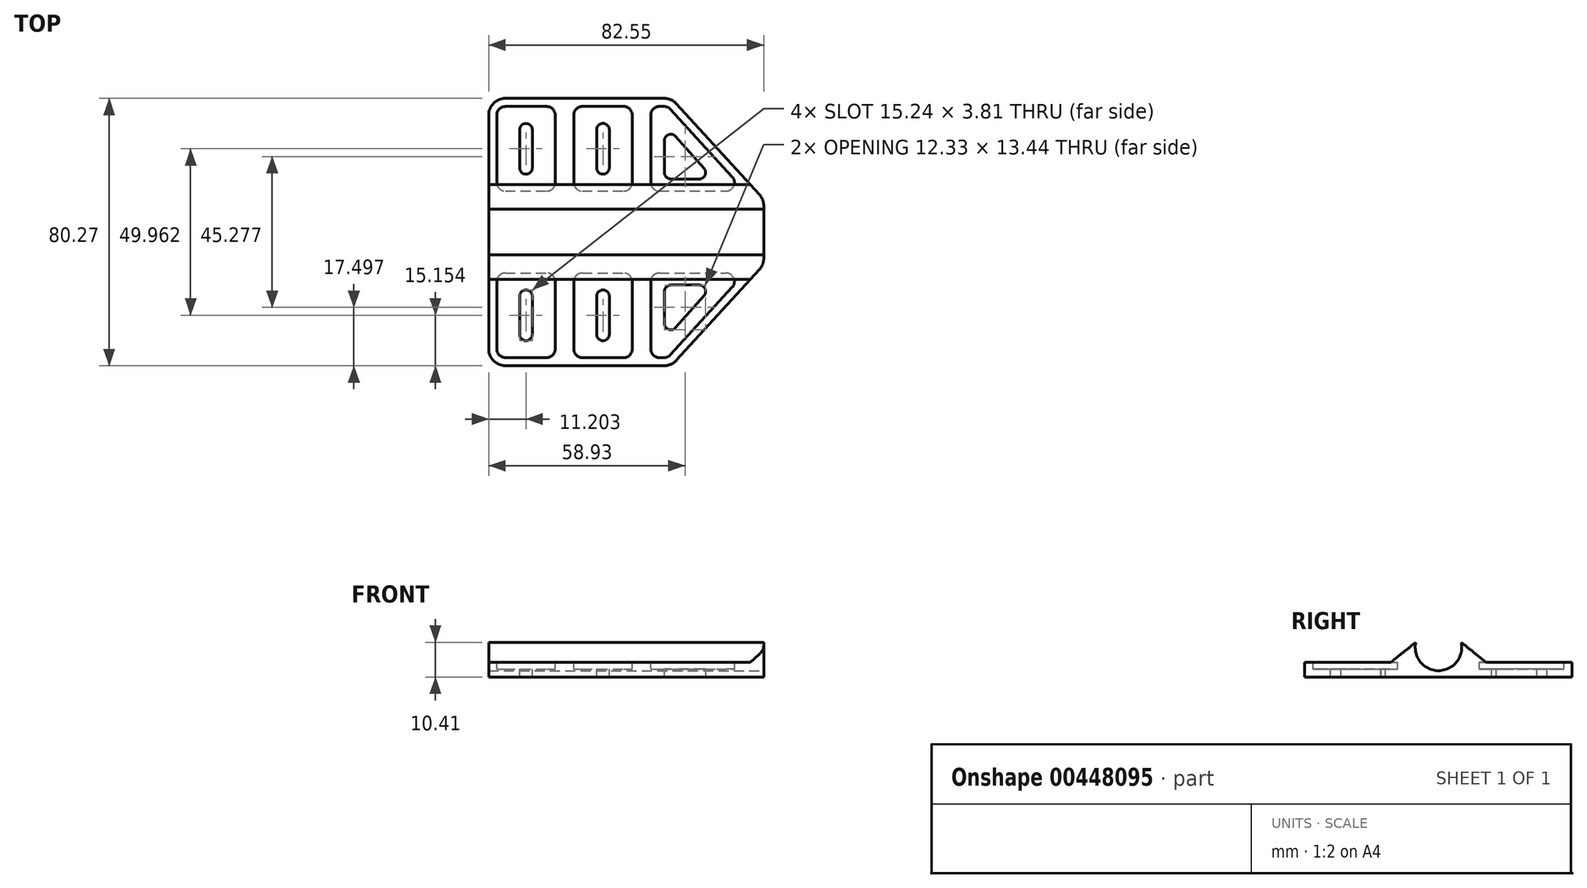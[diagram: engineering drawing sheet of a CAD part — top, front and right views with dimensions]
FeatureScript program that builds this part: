
annotation { "Feature Type Name" : "Feature", "Feature Type Description" : "" }
export const myFeature = defineFeature(function(context is Context, id is Id, definition is map)
    precondition{}
    {
        {
            var Q0;
            Q0=qCreatedBy(makeId("Top.planeOp"),FACE);
            var sketch = newSketch(context, id + "F0", { "sketchPlane" : qUnion([Q0])});
            skLineSegment(sketch, "E0.bottom", {"start": v(-50.59, 33.3) * mm, "end": v(4.28, 33.3) * mm});
            skLineSegment(sketch, "E0.top", {"start": v(-50.59, -46.96) * mm, "end": v(4.28, -46.96) * mm});
            skLineSegment(sketch, "E0.left", {"start": v(-50.59, 33.3) * mm, "end": v(-50.59, -46.96) * mm});
            skLineSegment(sketch, "E0.right", {"start": v(4.28, 33.3) * mm, "end": v(4.28, -46.96) * mm});
            skLineSegment(sketch, "E1", {"start": v(4.28, 3.02) * mm, "end": v(31.96, 3.02) * mm});
            skLineSegment(sketch, "E2", {"start": v(4.28, -16.67) * mm, "end": v(31.96, -16.67) * mm});
            skLineSegment(sketch, "E3", {"start": v(4.28, 33.3) * mm, "end": v(31.96, 3.02) * mm});
            skLineSegment(sketch, "E4", {"start": v(4.28, -46.96) * mm, "end": v(31.96, -16.67) * mm});
            skLineSegment(sketch, "E5", {"start": v(31.96, -16.67) * mm, "end": v(31.96, 3.02) * mm});
            skSolve(sketch);
        }
        {
            var Q0;
            Q0 = qSketchRegion(id + "F0", true);
            extrude(context, id + "F1", {"entities" : qUnion([Q0]), "depth" : 4.44 * mm});
        }
        {
            var Q0;
            Q0=makeQuery(id+"F1.opExtrude","CAP_FACE",FACE,{"disambiguationData":[OSD([sQuery(id+"F0.wireOp",EDGE,"E0.bottom"),sQuery(id+"F0.wireOp",EDGE,"E0.top"),sQuery(id+"F0.wireOp",EDGE,"E0.left"),sQuery(id+"F0.wireOp",EDGE,"E3"),sQuery(id+"F0.wireOp",EDGE,"E4"),sQuery(id+"F0.wireOp",EDGE,"E5")])],"isStart":false});
            var sketch = newSketch(context, id + "F2", { "sketchPlane" : qUnion([Q0])});
            skLineSegment(sketch, "E6", {"start": v(31.96, 3.02) * mm, "end": v(-50.59, 3.02) * mm});
            skLineSegment(sketch, "E7", {"start": v(31.96, -16.67) * mm, "end": v(-50.59, -16.67) * mm});
            skLineSegment(sketch, "E8", {"start": v(31.96, -6.83) * mm, "end": v(-50.59, -6.83) * mm});
            skSolve(sketch);
        }
        {
            var Q0;
            Q0=makeQuery(id+"F1.opExtrude","SWEPT_FACE",FACE,{"disambiguationData":[OSD([sQuery(id+"F0.wireOp",EDGE,"E5")])]});
            var sketch = newSketch(context, id + "F3", { "sketchPlane" : qUnion([Q0])});
            skCircle(sketch, "E9", {"center": v(-6.83, 8.9) * mm, "radius": 6.99 * mm});
            skPoint(sketch, "E9.centerSnap0", {"position": v(-6.83, 4.45) * mm});
            skSolve(sketch);
        }
        {
            var Q0;
            {var subQ0=sQuery(id+"F3.wireOp",EDGE,"E9");var subQ1=makeQuery(id+"F1.opExtrude","CAP_EDGE",EDGE,{"disambiguationData":[OSD([sQuery(id+"F0.wireOp",EDGE,"E5")])],"isStart":false});var subQ2=makeQuery(id+"F3.imprint","INTERSECT",VERTEX,{"disambiguationData":[OD(0.0)],"derivedFrom":[subQ1,subQ0]});Q0=makeQuery(id+"F3.imprint","IMPRINT",FACE,{"disambiguationData":[TD([[makeQuery(id+"F3.imprint","IMPRINT",EDGE,{"disambiguationData":[TD([[subQ2,-1.0]])],"derivedFrom":subQ0}),1.0]])]});}
            var Q1;
            {var subQ0=sQuery(id+"F3.wireOp",EDGE,"E9");var subQ1=makeQuery(id+"F1.opExtrude","CAP_EDGE",EDGE,{"disambiguationData":[OSD([sQuery(id+"F0.wireOp",EDGE,"E5")])],"isStart":false});var subQ2=makeQuery(id+"F3.imprint","INTERSECT",VERTEX,{"disambiguationData":[OD(0.0)],"derivedFrom":[subQ1,subQ0]});Q1=makeQuery(id+"F3.imprint","IMPRINT",FACE,{"disambiguationData":[TD([[makeQuery(id+"F3.imprint","IMPRINT",EDGE,{"disambiguationData":[TD([[subQ2,1.0]])],"derivedFrom":subQ0}),1.0]])]});}
            extrude(context, id + "F4", {"entities" : qUnion([Q0, Q1]), "operationType" : NewBodyOperationType.ADD, "oppositeDirection" : true, "depth" : 82.55 * mm});
        }
        {
            var Q0;
            Q0=makeQuery(id+"F4.boolean.opBoolean","INTERSECT",EDGE,{"disambiguationData":[OD(1.0)],"derivedFrom":[makeQuery(id+"F1.opExtrude","CAP_FACE",FACE,{"disambiguationData":[OSD([sQuery(id+"F0.wireOp",EDGE,"E0.bottom"),sQuery(id+"F0.wireOp",EDGE,"E0.top"),sQuery(id+"F0.wireOp",EDGE,"E0.left"),sQuery(id+"F0.wireOp",EDGE,"E3"),sQuery(id+"F0.wireOp",EDGE,"E4"),sQuery(id+"F0.wireOp",EDGE,"E5")])],"isStart":false}),makeQuery(id+"F4.opExtrude","SWEPT_FACE",FACE,{"disambiguationData":[OSD([sQuery(id+"F3.wireOp",EDGE,"E9")])]})]});
            var Q1;
            Q1=makeQuery(id+"F4.boolean.opBoolean","INTERSECT",EDGE,{"disambiguationData":[OD(0.0)],"derivedFrom":[makeQuery(id+"F1.opExtrude","CAP_FACE",FACE,{"disambiguationData":[OSD([sQuery(id+"F0.wireOp",EDGE,"E0.bottom"),sQuery(id+"F0.wireOp",EDGE,"E0.top"),sQuery(id+"F0.wireOp",EDGE,"E0.left"),sQuery(id+"F0.wireOp",EDGE,"E3"),sQuery(id+"F0.wireOp",EDGE,"E4"),sQuery(id+"F0.wireOp",EDGE,"E5")])],"isStart":false}),makeQuery(id+"F4.opExtrude","SWEPT_FACE",FACE,{"disambiguationData":[OSD([sQuery(id+"F3.wireOp",EDGE,"E9")])]})]});
            chamfer(context, id + "F5", {"entities" : qUnion([Q0, Q1]), "width" : 7.62 * mm, "tangentPropagation" : true});
        }
        {
            var Q0;
            Q0 = qSketchRegion(id + "F3", true);
            extrude(context, id + "F6", {"entities" : qUnion([Q0]), "operationType" : NewBodyOperationType.REMOVE, "oppositeDirection" : true, "depth" : 101.6 * mm});
        }
        {
            var Q0;
            {var subQ0=sQuery(id+"F2.wireOp",EDGE,"E7");Q0=makeQuery(id+"F2.imprint","IMPRINT",FACE,{"disambiguationData":[TD([[makeQuery(id+"F2.imprint","IMPRINT",EDGE,{"derivedFrom":subQ0}),1.0]])]});}
            var sketch = newSketch(context, id + "F7", { "sketchPlane" : qUnion([Q0])});
            skLineSegment(sketch, "E10.bottom", {"start": v(-48.15, -19.1) * mm, "end": v(-30.62, -19.1) * mm});
            skLineSegment(sketch, "E10.top", {"start": v(-48.15, -44.5) * mm, "end": v(-30.62, -44.5) * mm});
            skLineSegment(sketch, "E10.left", {"start": v(-48.15, -19.1) * mm, "end": v(-48.15, -44.5) * mm});
            skLineSegment(sketch, "E10.right", {"start": v(-30.62, -19.1) * mm, "end": v(-30.62, -44.5) * mm});
            skLineSegment(sketch, "E11.bottom", {"start": v(-25.04, -44.52) * mm, "end": v(-7.51, -44.52) * mm});
            skLineSegment(sketch, "E11.top", {"start": v(-25.04, -19.12) * mm, "end": v(-7.51, -19.12) * mm});
            skLineSegment(sketch, "E11.left", {"start": v(-25.04, -44.52) * mm, "end": v(-25.04, -19.12) * mm});
            skLineSegment(sketch, "E11.right", {"start": v(-7.51, -44.52) * mm, "end": v(-7.51, -19.12) * mm});
            skLineSegment(sketch, "E12", {"start": v(-1.92, -19.12) * mm, "end": v(-1.92, -44.52) * mm});
            skLineSegment(sketch, "E13", {"start": v(-1.92, -19.12) * mm, "end": v(26.42, -19.12) * mm});
            skLineSegment(sketch, "E14", {"start": v(-1.92, -44.52) * mm, "end": v(3.2, -44.52) * mm});
            skLineSegment(sketch, "E15", {"start": v(3.2, -44.52) * mm, "end": v(26.42, -19.12) * mm});
            skLineSegment(sketch, "E16.MirrorCS", {"start": v(-1.92, 30.87) * mm, "end": v(3.2, 30.87) * mm});
            skLineSegment(sketch, "E17.MirrorCS", {"start": v(-48.15, 30.86) * mm, "end": v(-30.62, 30.86) * mm});
            skLineSegment(sketch, "E18.MirrorCS", {"start": v(-48.15, 5.46) * mm, "end": v(-30.62, 5.46) * mm});
            skLineSegment(sketch, "E19.MirrorCS", {"start": v(-30.62, 5.46) * mm, "end": v(-30.62, 30.86) * mm});
            skLineSegment(sketch, "E20.MirrorCS", {"start": v(-1.92, 5.47) * mm, "end": v(26.42, 5.47) * mm});
            skLineSegment(sketch, "E21.MirrorCS", {"start": v(-1.92, 5.47) * mm, "end": v(-1.92, 30.87) * mm});
            skLineSegment(sketch, "E22.MirrorCS", {"start": v(-7.51, 30.87) * mm, "end": v(-7.51, 5.47) * mm});
            skLineSegment(sketch, "E23.MirrorCS", {"start": v(3.2, 30.87) * mm, "end": v(26.42, 5.47) * mm});
            skLineSegment(sketch, "E24.MirrorCS", {"start": v(-25.04, 30.87) * mm, "end": v(-7.51, 30.87) * mm});
            skLineSegment(sketch, "E25.MirrorCS", {"start": v(-48.15, 5.46) * mm, "end": v(-48.15, 30.86) * mm});
            skLineSegment(sketch, "E26.MirrorCS", {"start": v(-25.04, 5.47) * mm, "end": v(-7.51, 5.47) * mm});
            skLineSegment(sketch, "E27.MirrorCS", {"start": v(-25.04, 30.87) * mm, "end": v(-25.04, 5.47) * mm});
            skSolve(sketch);
        }
        {
            var Q0;
            Q0 = qSketchRegion(id + "F7", true);
            extrude(context, id + "F8", {"entities" : qUnion([Q0]), "operationType" : NewBodyOperationType.REMOVE, "oppositeDirection" : true, "depth" : 2.03 * mm});
        }
        {
            var Q0;
            Q0=makeQuery(id+"F8.boolean.opBoolean","COPY",EDGE,{"derivedFrom":makeQuery(id+"F8.opExtrude","SWEPT_EDGE",EDGE,{"disambiguationData":[OSD([sQuery(id+"F7.wireOp",EDGE,"E10.bottom"),sQuery(id+"F7.wireOp",EDGE,"E10.left")])]})});
            var Q1;
            Q1=makeQuery(id+"F8.boolean.opBoolean","COPY",EDGE,{"derivedFrom":makeQuery(id+"F8.opExtrude","SWEPT_EDGE",EDGE,{"disambiguationData":[OSD([sQuery(id+"F7.wireOp",EDGE,"E17.MirrorCS"),sQuery(id+"F7.wireOp",EDGE,"E25.MirrorCS")])]})});
            var Q2;
            Q2=makeQuery(id+"F8.boolean.opBoolean","COPY",EDGE,{"derivedFrom":makeQuery(id+"F8.opExtrude","SWEPT_EDGE",EDGE,{"disambiguationData":[OSD([sQuery(id+"F7.wireOp",EDGE,"E24.MirrorCS"),sQuery(id+"F7.wireOp",EDGE,"E27.MirrorCS")])]})});
            var Q3;
            Q3=makeQuery(id+"F8.boolean.opBoolean","COPY",EDGE,{"derivedFrom":makeQuery(id+"F8.opExtrude","SWEPT_EDGE",EDGE,{"disambiguationData":[OSD([sQuery(id+"F7.wireOp",EDGE,"E16.MirrorCS"),sQuery(id+"F7.wireOp",EDGE,"E21.MirrorCS")])]})});
            var Q4;
            Q4=makeQuery(id+"F8.boolean.opBoolean","COPY",EDGE,{"derivedFrom":makeQuery(id+"F8.opExtrude","SWEPT_EDGE",EDGE,{"disambiguationData":[OSD([sQuery(id+"F7.wireOp",EDGE,"E16.MirrorCS"),sQuery(id+"F7.wireOp",EDGE,"E23.MirrorCS")])]})});
            var Q5;
            Q5=makeQuery(id+"F8.boolean.opBoolean","COPY",EDGE,{"derivedFrom":makeQuery(id+"F8.opExtrude","SWEPT_EDGE",EDGE,{"disambiguationData":[OSD([sQuery(id+"F7.wireOp",EDGE,"E12"),sQuery(id+"F7.wireOp",EDGE,"E13")])]})});
            var Q6;
            Q6=makeQuery(id+"F8.boolean.opBoolean","COPY",EDGE,{"derivedFrom":makeQuery(id+"F8.opExtrude","SWEPT_EDGE",EDGE,{"disambiguationData":[OSD([sQuery(id+"F7.wireOp",EDGE,"E11.top"),sQuery(id+"F7.wireOp",EDGE,"E11.left")])]})});
            var Q7;
            Q7=makeQuery(id+"F8.boolean.opBoolean","COPY",EDGE,{"derivedFrom":makeQuery(id+"F8.opExtrude","SWEPT_EDGE",EDGE,{"disambiguationData":[OSD([sQuery(id+"F7.wireOp",EDGE,"E17.MirrorCS"),sQuery(id+"F7.wireOp",EDGE,"E19.MirrorCS")])]})});
            var Q8;
            Q8=makeQuery(id+"F8.boolean.opBoolean","COPY",EDGE,{"derivedFrom":makeQuery(id+"F8.opExtrude","SWEPT_EDGE",EDGE,{"disambiguationData":[OSD([sQuery(id+"F7.wireOp",EDGE,"E22.MirrorCS"),sQuery(id+"F7.wireOp",EDGE,"E24.MirrorCS")])]})});
            var Q9;
            Q9=makeQuery(id+"F8.boolean.opBoolean","COPY",EDGE,{"derivedFrom":makeQuery(id+"F8.opExtrude","SWEPT_EDGE",EDGE,{"disambiguationData":[OSD([sQuery(id+"F7.wireOp",EDGE,"E13"),sQuery(id+"F7.wireOp",EDGE,"E15")])]})});
            var Q10;
            Q10=makeQuery(id+"F8.boolean.opBoolean","COPY",EDGE,{"derivedFrom":makeQuery(id+"F8.opExtrude","SWEPT_EDGE",EDGE,{"disambiguationData":[OSD([sQuery(id+"F7.wireOp",EDGE,"E11.top"),sQuery(id+"F7.wireOp",EDGE,"E11.right")])]})});
            var Q11;
            Q11=makeQuery(id+"F8.boolean.opBoolean","COPY",EDGE,{"derivedFrom":makeQuery(id+"F8.opExtrude","SWEPT_EDGE",EDGE,{"disambiguationData":[OSD([sQuery(id+"F7.wireOp",EDGE,"E10.bottom"),sQuery(id+"F7.wireOp",EDGE,"E10.right")])]})});
            var Q12;
            Q12=makeQuery(id+"F8.boolean.opBoolean","COPY",EDGE,{"derivedFrom":makeQuery(id+"F8.opExtrude","SWEPT_EDGE",EDGE,{"disambiguationData":[OSD([sQuery(id+"F7.wireOp",EDGE,"E14"),sQuery(id+"F7.wireOp",EDGE,"E15")])]})});
            var Q13;
            Q13=makeQuery(id+"F8.boolean.opBoolean","COPY",EDGE,{"derivedFrom":makeQuery(id+"F8.opExtrude","SWEPT_EDGE",EDGE,{"disambiguationData":[OSD([sQuery(id+"F7.wireOp",EDGE,"E11.bottom"),sQuery(id+"F7.wireOp",EDGE,"E11.right")])]})});
            var Q14;
            Q14=makeQuery(id+"F8.boolean.opBoolean","COPY",EDGE,{"derivedFrom":makeQuery(id+"F8.opExtrude","SWEPT_EDGE",EDGE,{"disambiguationData":[OSD([sQuery(id+"F7.wireOp",EDGE,"E10.top"),sQuery(id+"F7.wireOp",EDGE,"E10.right")])]})});
            var Q15;
            Q15=makeQuery(id+"F8.boolean.opBoolean","COPY",EDGE,{"derivedFrom":makeQuery(id+"F8.opExtrude","SWEPT_EDGE",EDGE,{"disambiguationData":[OSD([sQuery(id+"F7.wireOp",EDGE,"E22.MirrorCS"),sQuery(id+"F7.wireOp",EDGE,"E26.MirrorCS")])]})});
            var Q16;
            Q16=makeQuery(id+"F8.boolean.opBoolean","COPY",EDGE,{"derivedFrom":makeQuery(id+"F8.opExtrude","SWEPT_EDGE",EDGE,{"disambiguationData":[OSD([sQuery(id+"F7.wireOp",EDGE,"E18.MirrorCS"),sQuery(id+"F7.wireOp",EDGE,"E19.MirrorCS")])]})});
            var Q17;
            Q17=makeQuery(id+"F8.boolean.opBoolean","COPY",EDGE,{"derivedFrom":makeQuery(id+"F8.opExtrude","SWEPT_EDGE",EDGE,{"disambiguationData":[OSD([sQuery(id+"F7.wireOp",EDGE,"E18.MirrorCS"),sQuery(id+"F7.wireOp",EDGE,"E25.MirrorCS")])]})});
            var Q18;
            Q18=makeQuery(id+"F8.boolean.opBoolean","COPY",EDGE,{"derivedFrom":makeQuery(id+"F8.opExtrude","SWEPT_EDGE",EDGE,{"disambiguationData":[OSD([sQuery(id+"F7.wireOp",EDGE,"E10.top"),sQuery(id+"F7.wireOp",EDGE,"E10.left")])]})});
            var Q19;
            Q19=makeQuery(id+"F8.boolean.opBoolean","COPY",EDGE,{"derivedFrom":makeQuery(id+"F8.opExtrude","SWEPT_EDGE",EDGE,{"disambiguationData":[OSD([sQuery(id+"F7.wireOp",EDGE,"E11.bottom"),sQuery(id+"F7.wireOp",EDGE,"E11.left")])]})});
            var Q20;
            Q20=makeQuery(id+"F8.boolean.opBoolean","COPY",EDGE,{"derivedFrom":makeQuery(id+"F8.opExtrude","SWEPT_EDGE",EDGE,{"disambiguationData":[OSD([sQuery(id+"F7.wireOp",EDGE,"E12"),sQuery(id+"F7.wireOp",EDGE,"E14")])]})});
            var Q21;
            Q21=makeQuery(id+"F8.boolean.opBoolean","COPY",EDGE,{"derivedFrom":makeQuery(id+"F8.opExtrude","SWEPT_EDGE",EDGE,{"disambiguationData":[OSD([sQuery(id+"F7.wireOp",EDGE,"E20.MirrorCS"),sQuery(id+"F7.wireOp",EDGE,"E21.MirrorCS")])]})});
            var Q22;
            Q22=makeQuery(id+"F8.boolean.opBoolean","COPY",EDGE,{"derivedFrom":makeQuery(id+"F8.opExtrude","SWEPT_EDGE",EDGE,{"disambiguationData":[OSD([sQuery(id+"F7.wireOp",EDGE,"E26.MirrorCS"),sQuery(id+"F7.wireOp",EDGE,"E27.MirrorCS")])]})});
            var Q23;
            Q23=makeQuery(id+"F8.boolean.opBoolean","COPY",EDGE,{"derivedFrom":makeQuery(id+"F8.opExtrude","SWEPT_EDGE",EDGE,{"disambiguationData":[OSD([sQuery(id+"F7.wireOp",EDGE,"E20.MirrorCS"),sQuery(id+"F7.wireOp",EDGE,"E23.MirrorCS")])]})});
            fillet(context, id + "F9", {"entities" : qUnion([Q0, Q1, Q2, Q3, Q4, Q5, Q6, Q7, Q8, Q9, Q10, Q11, Q12, Q13, Q14, Q15, Q16, Q17, Q18, Q19, Q20, Q21, Q22, Q23]), "radius" : 2.54 * mm, "tangentPropagation" : true, "allowEdgeOverflow" : false});
        }
        {
            var Q0;
            {var subQ0=sQuery(id+"F2.wireOp",EDGE,"E7");Q0=makeQuery(id+"F2.imprint","IMPRINT",FACE,{"disambiguationData":[TD([[makeQuery(id+"F2.imprint","IMPRINT",EDGE,{"derivedFrom":subQ0}),1.0]])]});}
            var sketch = newSketch(context, id + "F10", { "sketchPlane" : qUnion([Q0])});
            skLineSegment(sketch, "E28.bottom", {"start": v(-41.3, -24.19) * mm, "end": v(-37.48, -24.19) * mm});
            skLineSegment(sketch, "E28.top", {"start": v(-41.3, -39.43) * mm, "end": v(-37.48, -39.43) * mm});
            skLineSegment(sketch, "E28.left", {"start": v(-41.3, -24.19) * mm, "end": v(-41.3, -39.43) * mm});
            skLineSegment(sketch, "E28.right", {"start": v(-37.48, -24.19) * mm, "end": v(-37.48, -39.43) * mm});
            skLineSegment(sketch, "E29.bottom", {"start": v(-18.18, -24.2) * mm, "end": v(-14.37, -24.2) * mm});
            skLineSegment(sketch, "E29.top", {"start": v(-18.18, -39.44) * mm, "end": v(-14.37, -39.44) * mm});
            skLineSegment(sketch, "E29.left", {"start": v(-18.18, -24.2) * mm, "end": v(-18.18, -39.44) * mm});
            skLineSegment(sketch, "E29.right", {"start": v(-14.37, -24.2) * mm, "end": v(-14.37, -39.44) * mm});
            skLineSegment(sketch, "E30", {"start": v(2.17, -22.74) * mm, "end": v(16.85, -22.74) * mm});
            skLineSegment(sketch, "E31", {"start": v(16.85, -22.74) * mm, "end": v(2.17, -39.3) * mm});
            skLineSegment(sketch, "E32", {"start": v(2.17, -39.3) * mm, "end": v(2.17, -22.74) * mm});
            skLineSegment(sketch, "E33.MirrorCS", {"start": v(2.17, 25.66) * mm, "end": v(2.17, 9.1) * mm});
            skLineSegment(sketch, "E34.MirrorCS", {"start": v(16.85, 9.1) * mm, "end": v(2.17, 25.66) * mm});
            skLineSegment(sketch, "E35.MirrorCS", {"start": v(2.17, 9.1) * mm, "end": v(16.85, 9.1) * mm});
            skLineSegment(sketch, "E36.MirrorCS", {"start": v(-14.37, 10.55) * mm, "end": v(-14.37, 25.79) * mm});
            skLineSegment(sketch, "E37.MirrorCS", {"start": v(-18.18, 10.55) * mm, "end": v(-18.18, 25.79) * mm});
            skLineSegment(sketch, "E38.MirrorCS", {"start": v(-18.18, 25.79) * mm, "end": v(-14.37, 25.79) * mm});
            skLineSegment(sketch, "E39.MirrorCS", {"start": v(-41.3, 10.54) * mm, "end": v(-41.3, 25.78) * mm});
            skLineSegment(sketch, "E40.MirrorCS", {"start": v(-41.3, 25.78) * mm, "end": v(-37.48, 25.78) * mm});
            skLineSegment(sketch, "E41.MirrorCS", {"start": v(-41.3, 10.54) * mm, "end": v(-37.48, 10.54) * mm});
            skLineSegment(sketch, "E42.MirrorCS", {"start": v(-18.18, 10.55) * mm, "end": v(-14.37, 10.55) * mm});
            skLineSegment(sketch, "E43.MirrorCS", {"start": v(-37.48, 10.54) * mm, "end": v(-37.48, 25.78) * mm});
            skSolve(sketch);
        }
        {
            var Q0;
            Q0 = qSketchRegion(id + "F10", true);
            extrude(context, id + "F11", {"entities" : qUnion([Q0]), "operationType" : NewBodyOperationType.REMOVE, "oppositeDirection" : true, "depth" : 25.4 * mm});
        }
        {
            var Q0;
            Q0=makeQuery(id+"F11.boolean.opBoolean","COPY",EDGE,{"derivedFrom":makeQuery(id+"F11.opExtrude","SWEPT_EDGE",EDGE,{"disambiguationData":[OSD([sQuery(id+"F10.wireOp",EDGE,"E28.bottom"),sQuery(id+"F10.wireOp",EDGE,"E28.left")])]})});
            var Q1;
            Q1=makeQuery(id+"F11.boolean.opBoolean","COPY",EDGE,{"derivedFrom":makeQuery(id+"F11.opExtrude","SWEPT_EDGE",EDGE,{"disambiguationData":[OSD([sQuery(id+"F10.wireOp",EDGE,"E28.bottom"),sQuery(id+"F10.wireOp",EDGE,"E28.right")])]})});
            var Q2;
            Q2=makeQuery(id+"F11.boolean.opBoolean","COPY",EDGE,{"derivedFrom":makeQuery(id+"F11.opExtrude","SWEPT_EDGE",EDGE,{"disambiguationData":[OSD([sQuery(id+"F10.wireOp",EDGE,"E29.bottom"),sQuery(id+"F10.wireOp",EDGE,"E29.right")])]})});
            var Q3;
            Q3=makeQuery(id+"F11.boolean.opBoolean","COPY",EDGE,{"derivedFrom":makeQuery(id+"F11.opExtrude","SWEPT_EDGE",EDGE,{"disambiguationData":[OSD([sQuery(id+"F10.wireOp",EDGE,"E30"),sQuery(id+"F10.wireOp",EDGE,"E31")])]})});
            var Q4;
            Q4=makeQuery(id+"F11.boolean.opBoolean","COPY",EDGE,{"derivedFrom":makeQuery(id+"F11.opExtrude","SWEPT_EDGE",EDGE,{"disambiguationData":[OSD([sQuery(id+"F10.wireOp",EDGE,"E36.MirrorCS"),sQuery(id+"F10.wireOp",EDGE,"E38.MirrorCS")])]})});
            var Q5;
            Q5=makeQuery(id+"F11.boolean.opBoolean","COPY",EDGE,{"derivedFrom":makeQuery(id+"F11.opExtrude","SWEPT_EDGE",EDGE,{"disambiguationData":[OSD([sQuery(id+"F10.wireOp",EDGE,"E40.MirrorCS"),sQuery(id+"F10.wireOp",EDGE,"E43.MirrorCS")])]})});
            var Q6;
            Q6=makeQuery(id+"F11.boolean.opBoolean","COPY",EDGE,{"derivedFrom":makeQuery(id+"F11.opExtrude","SWEPT_EDGE",EDGE,{"disambiguationData":[OSD([sQuery(id+"F10.wireOp",EDGE,"E29.bottom"),sQuery(id+"F10.wireOp",EDGE,"E29.left")])]})});
            var Q7;
            Q7=makeQuery(id+"F11.boolean.opBoolean","COPY",EDGE,{"derivedFrom":makeQuery(id+"F11.opExtrude","SWEPT_EDGE",EDGE,{"disambiguationData":[OSD([sQuery(id+"F10.wireOp",EDGE,"E30"),sQuery(id+"F10.wireOp",EDGE,"E32")])]})});
            var Q8;
            Q8=makeQuery(id+"F11.boolean.opBoolean","COPY",EDGE,{"derivedFrom":makeQuery(id+"F11.opExtrude","SWEPT_EDGE",EDGE,{"disambiguationData":[OSD([sQuery(id+"F10.wireOp",EDGE,"E37.MirrorCS"),sQuery(id+"F10.wireOp",EDGE,"E38.MirrorCS")])]})});
            var Q9;
            Q9=makeQuery(id+"F11.boolean.opBoolean","COPY",EDGE,{"derivedFrom":makeQuery(id+"F11.opExtrude","SWEPT_EDGE",EDGE,{"disambiguationData":[OSD([sQuery(id+"F10.wireOp",EDGE,"E39.MirrorCS"),sQuery(id+"F10.wireOp",EDGE,"E40.MirrorCS")])]})});
            var Q10;
            Q10=makeQuery(id+"F11.boolean.opBoolean","COPY",EDGE,{"derivedFrom":makeQuery(id+"F11.opExtrude","SWEPT_EDGE",EDGE,{"disambiguationData":[OSD([sQuery(id+"F10.wireOp",EDGE,"E33.MirrorCS"),sQuery(id+"F10.wireOp",EDGE,"E34.MirrorCS")])]})});
            var Q11;
            Q11=makeQuery(id+"F11.boolean.opBoolean","COPY",EDGE,{"derivedFrom":makeQuery(id+"F11.opExtrude","SWEPT_EDGE",EDGE,{"disambiguationData":[OSD([sQuery(id+"F10.wireOp",EDGE,"E28.top"),sQuery(id+"F10.wireOp",EDGE,"E28.left")])]})});
            var Q12;
            Q12=makeQuery(id+"F11.boolean.opBoolean","COPY",EDGE,{"derivedFrom":makeQuery(id+"F11.opExtrude","SWEPT_EDGE",EDGE,{"disambiguationData":[OSD([sQuery(id+"F10.wireOp",EDGE,"E29.top"),sQuery(id+"F10.wireOp",EDGE,"E29.left")])]})});
            var Q13;
            Q13=makeQuery(id+"F11.boolean.opBoolean","COPY",EDGE,{"derivedFrom":makeQuery(id+"F11.opExtrude","SWEPT_EDGE",EDGE,{"disambiguationData":[OSD([sQuery(id+"F10.wireOp",EDGE,"E39.MirrorCS"),sQuery(id+"F10.wireOp",EDGE,"E41.MirrorCS")])]})});
            var Q14;
            Q14=makeQuery(id+"F11.boolean.opBoolean","COPY",EDGE,{"derivedFrom":makeQuery(id+"F11.opExtrude","SWEPT_EDGE",EDGE,{"disambiguationData":[OSD([sQuery(id+"F10.wireOp",EDGE,"E37.MirrorCS"),sQuery(id+"F10.wireOp",EDGE,"E42.MirrorCS")])]})});
            var Q15;
            Q15=makeQuery(id+"F11.boolean.opBoolean","COPY",EDGE,{"derivedFrom":makeQuery(id+"F11.opExtrude","SWEPT_EDGE",EDGE,{"disambiguationData":[OSD([sQuery(id+"F10.wireOp",EDGE,"E33.MirrorCS"),sQuery(id+"F10.wireOp",EDGE,"E35.MirrorCS")])]})});
            var Q16;
            Q16=makeQuery(id+"F11.boolean.opBoolean","COPY",EDGE,{"derivedFrom":makeQuery(id+"F11.opExtrude","SWEPT_EDGE",EDGE,{"disambiguationData":[OSD([sQuery(id+"F10.wireOp",EDGE,"E29.top"),sQuery(id+"F10.wireOp",EDGE,"E29.right")])]})});
            var Q17;
            Q17=makeQuery(id+"F11.boolean.opBoolean","COPY",EDGE,{"derivedFrom":makeQuery(id+"F11.opExtrude","SWEPT_EDGE",EDGE,{"disambiguationData":[OSD([sQuery(id+"F10.wireOp",EDGE,"E28.top"),sQuery(id+"F10.wireOp",EDGE,"E28.right")])]})});
            var Q18;
            Q18=makeQuery(id+"F11.boolean.opBoolean","COPY",EDGE,{"derivedFrom":makeQuery(id+"F11.opExtrude","SWEPT_EDGE",EDGE,{"disambiguationData":[OSD([sQuery(id+"F10.wireOp",EDGE,"E36.MirrorCS"),sQuery(id+"F10.wireOp",EDGE,"E42.MirrorCS")])]})});
            var Q19;
            Q19=makeQuery(id+"F11.boolean.opBoolean","COPY",EDGE,{"derivedFrom":makeQuery(id+"F11.opExtrude","SWEPT_EDGE",EDGE,{"disambiguationData":[OSD([sQuery(id+"F10.wireOp",EDGE,"E41.MirrorCS"),sQuery(id+"F10.wireOp",EDGE,"E43.MirrorCS")])]})});
            var Q20;
            Q20=makeQuery(id+"F11.boolean.opBoolean","COPY",EDGE,{"derivedFrom":makeQuery(id+"F11.opExtrude","SWEPT_EDGE",EDGE,{"disambiguationData":[OSD([sQuery(id+"F10.wireOp",EDGE,"E34.MirrorCS"),sQuery(id+"F10.wireOp",EDGE,"E35.MirrorCS")])]})});
            var Q21;
            Q21=makeQuery(id+"F11.boolean.opBoolean","COPY",EDGE,{"derivedFrom":makeQuery(id+"F11.opExtrude","SWEPT_EDGE",EDGE,{"disambiguationData":[OSD([sQuery(id+"F10.wireOp",EDGE,"E31"),sQuery(id+"F10.wireOp",EDGE,"E32")])]})});
            fillet(context, id + "F12", {"entities" : qUnion([Q0, Q1, Q2, Q3, Q4, Q5, Q6, Q7, Q8, Q9, Q10, Q11, Q12, Q13, Q14, Q15, Q16, Q17, Q18, Q19, Q20, Q21]), "radius" : 1.9 * mm, "tangentPropagation" : true, "allowEdgeOverflow" : false});
        }
        {
            var Q0;
            Q0=makeQuery(id+"F1.opExtrude","SWEPT_EDGE",EDGE,{"disambiguationData":[OSD([sQuery(id+"F0.wireOp",EDGE,"E0.top"),sQuery(id+"F0.wireOp",EDGE,"E0.left")])]});
            var Q1;
            Q1=makeQuery(id+"F1.opExtrude","SWEPT_EDGE",EDGE,{"disambiguationData":[OSD([sQuery(id+"F0.wireOp",EDGE,"E0.top"),sQuery(id+"F0.wireOp",EDGE,"E0.right"),sQuery(id+"F0.wireOp",EDGE,"E4")])]});
            var Q2;
            Q2=makeQuery(id+"F1.opExtrude","SWEPT_EDGE",EDGE,{"disambiguationData":[OSD([sQuery(id+"F0.wireOp",EDGE,"E2"),sQuery(id+"F0.wireOp",EDGE,"E4"),sQuery(id+"F0.wireOp",EDGE,"E5")])]});
            var Q3;
            Q3=makeQuery(id+"F1.opExtrude","SWEPT_EDGE",EDGE,{"disambiguationData":[OSD([sQuery(id+"F0.wireOp",EDGE,"E1"),sQuery(id+"F0.wireOp",EDGE,"E3"),sQuery(id+"F0.wireOp",EDGE,"E5")])]});
            var Q4;
            Q4=makeQuery(id+"F1.opExtrude","SWEPT_EDGE",EDGE,{"disambiguationData":[OSD([sQuery(id+"F0.wireOp",EDGE,"E0.bottom"),sQuery(id+"F0.wireOp",EDGE,"E0.right"),sQuery(id+"F0.wireOp",EDGE,"E3")])]});
            var Q5;
            Q5=makeQuery(id+"F1.opExtrude","SWEPT_EDGE",EDGE,{"disambiguationData":[OSD([sQuery(id+"F0.wireOp",EDGE,"E0.bottom"),sQuery(id+"F0.wireOp",EDGE,"E0.left")])]});
            fillet(context, id + "F13", {"entities" : qUnion([Q0, Q1, Q2, Q3, Q4, Q5]), "radius" : 5.08 * mm, "tangentPropagation" : true, "allowEdgeOverflow" : false});
        }
    });
